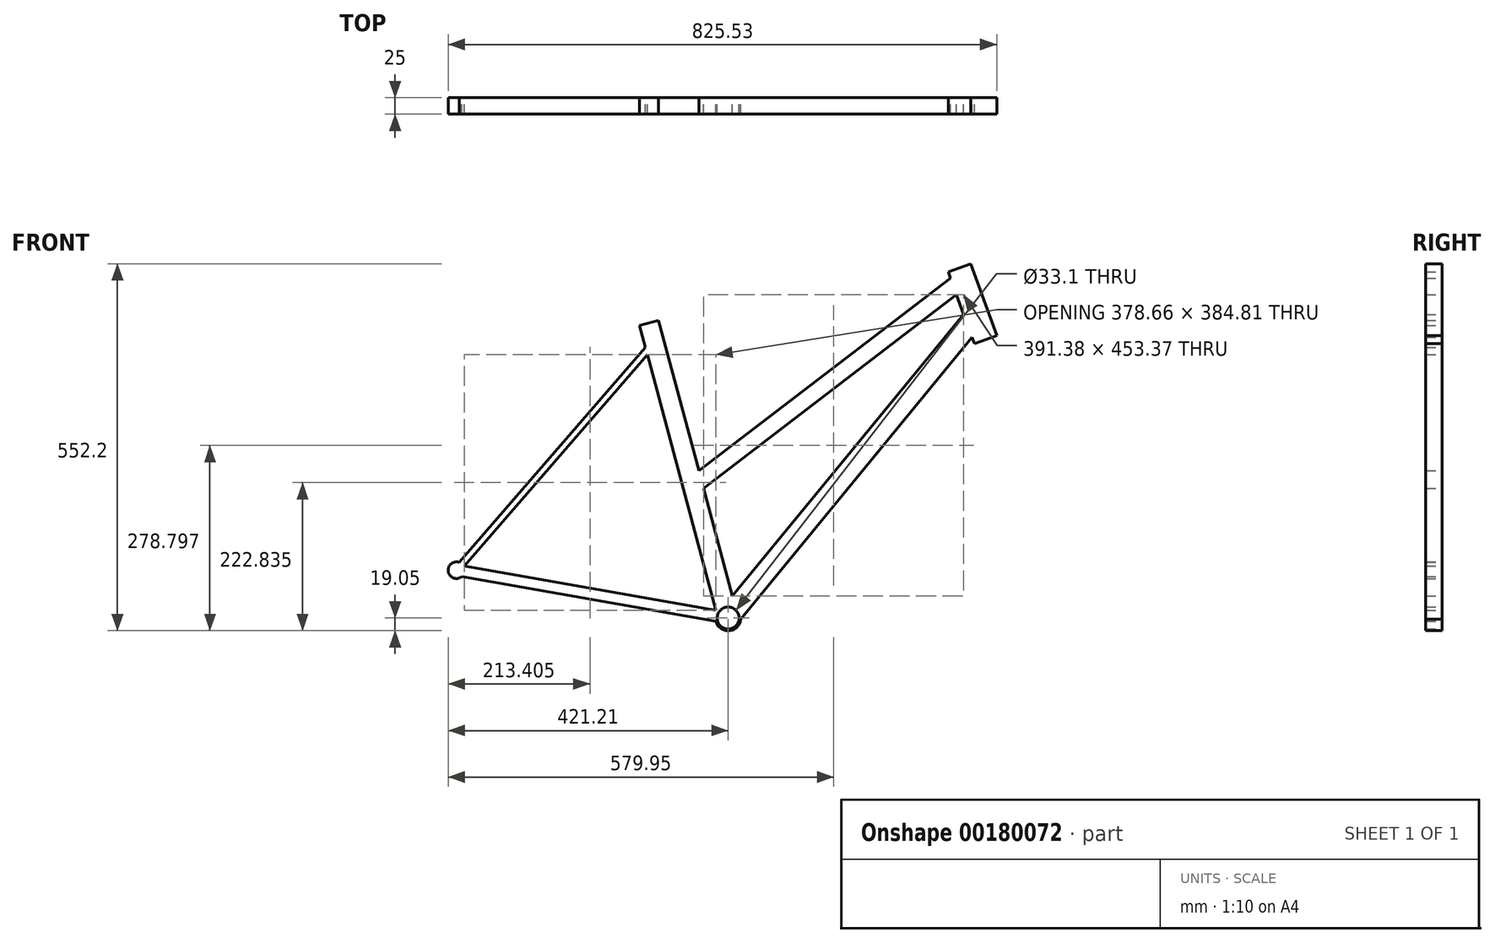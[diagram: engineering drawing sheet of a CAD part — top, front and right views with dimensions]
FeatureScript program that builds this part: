
annotation { "Feature Type Name" : "Feature", "Feature Type Description" : "" }
export const myFeature = defineFeature(function(context is Context, id is Id, definition is map)
    precondition{}
    {
        {
            var Q0;
            Q0=qCreatedBy(makeId("Front.planeOp"),FACE);
            var sketch = newSketch(context, id + "F1", { "sketchPlane" : qUnion([Q0])});
            skCircle(sketch, "E0", {"center": v(0, 0) * mm, "radius": 19.05 * mm});
            skLineSegment(sketch, "E1", {"start": v(0, 0) * mm, "end": v(-145.66, 0) * mm, "construction": true});
            skLineSegment(sketch, "E2", {"start": v(0, 0) * mm, "end": v(0, 415.35) * mm, "construction": true});
            skLineSegment(sketch, "E3", {"start": v(-408.7, 72) * mm, "end": v(0, 72) * mm, "construction": true});
            skLineSegment(sketch, "E4", {"start": v(0, 0) * mm, "end": v(-111.3, 415.35) * mm, "construction": true});
            skLineSegment(sketch, "E5", {"start": v(-408.7, 72) * mm, "end": v(0, 0) * mm, "construction": true});
            skLineSegment(sketch, "E6", {"start": v(-408.7, 72) * mm, "end": v(-111.3, 415.35) * mm, "construction": true});
            skLineSegment(sketch, "E7", {"start": v(0, 72) * mm, "end": v(558.68, 72) * mm, "construction": true});
            skLineSegment(sketch, "E8", {"start": v(513.68, 72) * mm, "end": v(392.53, 404.84) * mm, "construction": true});
            skLineSegment(sketch, "E9", {"start": v(-111.3, 415.35) * mm, "end": v(-95.87, 415.35) * mm, "construction": true});
            skLineSegment(sketch, "E10", {"start": v(558.68, 72) * mm, "end": v(392.53, 404.84) * mm, "construction": true});
            skLineSegment(sketch, "E11", {"start": v(387.4, 418.93) * mm, "end": v(388.7, 415.35) * mm});
            skLineSegment(sketch, "E12", {"start": v(387.4, 418.93) * mm, "end": v(392.53, 404.84) * mm, "construction": true});
            skLineSegment(sketch, "E13", {"start": v(-111.3, 415.35) * mm, "end": v(-119.06, 444.33) * mm, "construction": true});
            skLineSegment(sketch, "E14", {"start": v(388.7, 415.35) * mm, "end": v(348.07, 527) * mm, "construction": true});
            skLineSegment(sketch, "E15", {"start": v(374.02, 455.7) * mm, "end": v(0, 0) * mm, "construction": true});
            skLineSegment(sketch, "E16.0", {"start": v(391.23, 461.04) * mm, "end": v(364.99, 533.15) * mm});
            skLineSegment(sketch, "E16.1", {"start": v(391.23, 461.04) * mm, "end": v(404.32, 425.09) * mm});
            skLineSegment(sketch, "E17.0", {"start": v(358.56, 445.55) * mm, "end": v(370.49, 412.78) * mm});
            skLineSegment(sketch, "E17.1", {"start": v(358.56, 445.55) * mm, "end": v(331.16, 520.84) * mm});
            skLineSegment(sketch, "E18", {"start": v(331.16, 520.84) * mm, "end": v(364.99, 533.15) * mm});
            skLineSegment(sketch, "E19", {"start": v(370.49, 412.78) * mm, "end": v(404.32, 425.09) * mm});
            skLineSegment(sketch, "E20.1", {"start": v(11.32, 15.32) * mm, "end": v(-104.66, 448.18) * mm});
            skLineSegment(sketch, "E21.1", {"start": v(-17.46, 7.6) * mm, "end": v(-133.45, 440.47) * mm});
            skLineSegment(sketch, "E22", {"start": v(-133.45, 440.47) * mm, "end": v(-104.66, 448.18) * mm});
            skLineSegment(sketch, "E23.trimOffspring", {"start": v(369.55, 415.35) * mm, "end": v(388.7, 415.35) * mm, "construction": true});
            skLineSegment(sketch, "E24", {"start": v(354.11, 510.4) * mm, "end": v(-40.5, 208.73) * mm, "construction": true});
            skLineSegment(sketch, "E25.0", {"start": v(334.58, 511.44) * mm, "end": v(-44.06, 222) * mm});
            skLineSegment(sketch, "E26.0", {"start": v(354.43, 456.9) * mm, "end": v(6.57, 33.06) * mm});
            skLineSegment(sketch, "E27.trimOffspring", {"start": v(367.07, 422.17) * mm, "end": v(18.95, -1.98) * mm});
            skLineSegment(sketch, "E28.trimOffspring", {"start": v(343.68, 486.43) * mm, "end": v(-36.95, 195.47) * mm});
            skLineSegment(sketch, "E29.trimOffspring", {"start": v(-5.06, 18.9) * mm, "end": v(-5.63, 18.2) * mm});
            skCircle(sketch, "E30", {"center": v(-408.7, 72) * mm, "radius": 311 * mm});
            skCircle(sketch, "E31", {"center": v(558.68, 72) * mm, "radius": 311 * mm});
            skCircle(sketch, "E32", {"center": v(-408.7, 72) * mm, "radius": 343 * mm});
            skCircle(sketch, "E33", {"center": v(558.68, 72) * mm, "radius": 343 * mm});
            skLineSegment(sketch, "E34", {"start": v(68.72, 108.79) * mm, "end": v(197.63, 265.86) * mm});
            skLineSegment(sketch, "E35", {"start": v(197.63, 265.86) * mm, "end": v(128.92, 322.26) * mm});
            skLineSegment(sketch, "E36", {"start": v(128.92, 322.26) * mm, "end": v(0, 165.19) * mm});
            skLineSegment(sketch, "E37", {"start": v(0, 165.19) * mm, "end": v(68.72, 108.79) * mm});
            skLineSegment(sketch, "E38.0", {"start": v(-400.64, 62.45) * mm, "end": v(-18.41, -4.88) * mm});
            skLineSegment(sketch, "E39.trimOffspring", {"start": v(-397.14, 78.08) * mm, "end": v(-18.47, 11.38) * mm});
            skLineSegment(sketch, "E40.trimOffspring", {"start": v(-397.14, 78.08) * mm, "end": v(-121.58, 396.2) * mm});
            skCircle(sketch, "E41", {"center": v(-408.7, 72) * mm, "radius": 12.5 * mm});
            skLineSegment(sketch, "E42.trimOffspring", {"start": v(-404.74, 83.85) * mm, "end": v(-124.56, 407.3) * mm});
            skCircle(sketch, "E43", {"center": v(0, 0) * mm, "radius": 16.55 * mm});
            skLineSegment(sketch, "E44", {"start": v(-40.5, 208.73) * mm, "end": v(-53.3, 198.95) * mm, "construction": true});
            skSolve(sketch);
        }
        {
            var Q0;
            {var subQ0=sQuery(id+"F1.wireOp",EDGE,"E40.trimOffspring");var subQ1=sQuery(id+"F1.wireOp",EDGE,"E21.1");var subQ2=makeQuery(id+"F1.imprint","INTERSECT",VERTEX,{"derivedFrom":[subQ1,subQ0]});Q0=makeQuery(id+"F1.imprint","IMPRINT",FACE,{"disambiguationData":[TD([[makeQuery(id+"F1.imprint","IMPRINT",EDGE,{"disambiguationData":[TD([[subQ2,-1.0]])],"derivedFrom":subQ1}),1.0]])]});}
            var Q1;
            {var subQ0=sQuery(id+"F1.wireOp",EDGE,"E42.trimOffspring");var subQ1=sQuery(id+"F1.wireOp",EDGE,"E30");var subQ2=makeQuery(id+"F1.imprint","INTERSECT",VERTEX,{"derivedFrom":[subQ1,subQ0]});Q1=makeQuery(id+"F1.imprint","IMPRINT",FACE,{"disambiguationData":[TD([[makeQuery(id+"F1.imprint","IMPRINT",EDGE,{"disambiguationData":[TD([[subQ2,1.0]])],"derivedFrom":subQ1}),-1.0]])]});}
            var Q2;
            {var subQ3=sQuery(id+"F1.wireOp",EDGE,"E30");var subQ5=sQuery(id+"F1.wireOp",EDGE,"E42.trimOffspring");var subQ7=makeQuery(id+"F1.imprint","INTERSECT",VERTEX,{"derivedFrom":[subQ3,subQ5]});Q2=makeQuery(id+"F1.imprint","IMPRINT",FACE,{"disambiguationData":[TD([[makeQuery(id+"F1.imprint","IMPRINT",EDGE,{"disambiguationData":[TD([[subQ7,1.0]])],"derivedFrom":subQ3}),1.0]])]});}
            var Q3;
            {var subQ0=sQuery(id+"F1.wireOp",EDGE,"E22");Q3=makeQuery(id+"F1.imprint","IMPRINT",FACE,{"disambiguationData":[TD([[makeQuery(id+"F1.imprint","IMPRINT",EDGE,{"derivedFrom":subQ0}),-1.0]])]});}
            var Q4;
            {var subQ0=sQuery(id+"F1.wireOp",EDGE,"E41");var subQ1=makeQuery(id+"F1.imprint","INTERSECT",VERTEX,{"derivedFrom":[sQuery(id+"F1.wireOp",EDGE,"E38.0"),subQ0]});Q4=makeQuery(id+"F1.imprint","IMPRINT",FACE,{"disambiguationData":[TD([[makeQuery(id+"F1.imprint","IMPRINT",EDGE,{"disambiguationData":[TD([[subQ1,1.0]])],"derivedFrom":subQ0}),1.0]])]});}
            var Q5;
            {var subQ0=sQuery(id+"F1.wireOp",EDGE,"E38.0");var subQ1=sQuery(id+"F1.wireOp",EDGE,"E30");var subQ2=makeQuery(id+"F1.imprint","INTERSECT",VERTEX,{"derivedFrom":[subQ1,subQ0]});Q5=makeQuery(id+"F1.imprint","IMPRINT",FACE,{"disambiguationData":[TD([[makeQuery(id+"F1.imprint","IMPRINT",EDGE,{"disambiguationData":[TD([[subQ2,-1.0]])],"derivedFrom":subQ1}),-1.0]])]});}
            var Q6;
            {var subQ1=sQuery(id+"F1.wireOp",EDGE,"E0");var subQ5=sQuery(id+"F1.wireOp",EDGE,"E21.1");var subQ6=makeQuery(id+"F1.imprint","INTERSECT",VERTEX,{"derivedFrom":[subQ1,subQ5]});Q6=makeQuery(id+"F1.imprint","IMPRINT",FACE,{"disambiguationData":[TD([[makeQuery(id+"F1.imprint","IMPRINT",EDGE,{"disambiguationData":[TD([[subQ6,-1.0]])],"derivedFrom":subQ1}),-1.0]])]});}
            var Q7;
            {var subQ0=sQuery(id+"F1.wireOp",EDGE,"E0");var subQ4=makeQuery(id+"F1.imprint","IMPRINT",VERTEX,{"derivedFrom":subQ0});Q7=makeQuery(id+"F1.imprint","IMPRINT",FACE,{"disambiguationData":[TD([[makeQuery(id+"F1.imprint","IMPRINT",EDGE,{"disambiguationData":[TD([[subQ4,1.0]])],"derivedFrom":subQ0}),1.0]])]});}
            var Q8;
            {var subQ4=sQuery(id+"F1.wireOp",EDGE,"E25.0");Q8=makeQuery(id+"F1.imprint","IMPRINT",FACE,{"disambiguationData":[TD([[makeQuery(id+"F1.imprint","IMPRINT",EDGE,{"derivedFrom":subQ4}),1.0]])]});}
            var Q9;
            {var subQ9=sQuery(id+"F1.wireOp",EDGE,"E27.trimOffspring");Q9=makeQuery(id+"F1.imprint","IMPRINT",FACE,{"disambiguationData":[TD([[makeQuery(id+"F1.imprint","IMPRINT",EDGE,{"derivedFrom":subQ9}),-1.0]])]});}
            var Q10;
            Q10=makeQuery(id+"F1.imprint","IMPRINT",FACE,{"disambiguationData":[TD([[makeQuery(id+"F1.imprint","IMPRINT",EDGE,{"derivedFrom":sQuery(id+"F1.wireOp",EDGE,"E16.0")}),1.0]])]});
            extrude(context, id + "F0", {"entities" : qUnion([Q0, Q1, Q2, Q3, Q4, Q5, Q6, Q7, Q8, Q9, Q10]), "depth" : 25 * mm});
        }
    });
